# Revit family: Plumbing_Fixture-Bathtub-BainUltra-Evanescence-Oval-6636
name_source: partatom
category: Plumbing Fixtures
units: mm (PartAtom-declared; Revit-internal decimal feet)

## family parameters
Always vertical = Yes
Cut with Voids When Loaded = No
OmniClass Number = 23.45.05.14.21.17
OmniClass Title = Therapeutic Whirlpool Baths
Part Type = Normal
Room Calculation Point = No
Round Connector Dimension = Use Radius
Shared = No
Work Plane-Based = No

## types (1)
- 66" x 36"
    Apparent Load = 0 VA
    Assembly Code = D2010510
    CWFU = 0
    Capacity = 51
    Connector Description = ELECTRICAL CONNECTOR
    Country = United States
    Default Elevation = 0' - 0"
    Description = THERAPEUTIC BATH
    Drain Connector Description = SANITARY WASTE DRAIN
    Drain Diameter = 0' - 1 1/2"
    Drain Radius = 0' - 0 3/4"
    HWFU = 0
    Height = 2' - 4"
    Jets = Yes
    Length = 5' - 6"
    Lens Material = <By Category>
    Load Classification = Other
    Manufacturer = BainUltra
    Model = 6636
    Number of Poles = 1
    Other Region = No
    Power Factor = 1
    Product Documentation Link = http://www.bainultra.com
    Product Name = Evanescence
    Product Page URL = http://www.bainultra.com
    Product data url = https://bimobject.com
    Region = North America
    Series = Evanescence
    Shipping Weight = 230.00 kip
    URL = www.bainultra.com
    US Region = Yes
    Voltage = 120 V
    WFU = 4
    Water Flow = 0 GPM
    Width = 3' - 0"

## geometry (parser evidence)
native form markers: Blend x4, Sweep x16
no freeform markers — native parametric forms only
